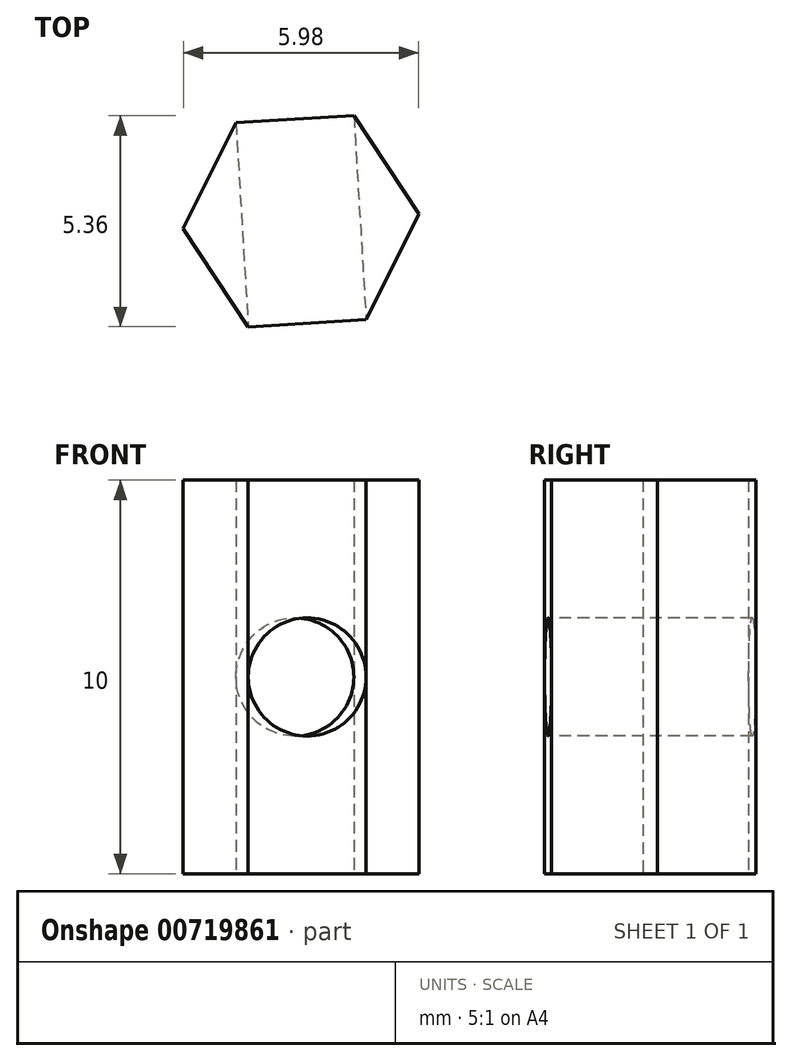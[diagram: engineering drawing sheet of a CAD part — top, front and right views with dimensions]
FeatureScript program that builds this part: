
annotation { "Feature Type Name" : "Feature", "Feature Type Description" : "" }
export const myFeature = defineFeature(function(context is Context, id is Id, definition is map)
    precondition{}
    {
        {
            var Q0;
            Q0=qCreatedBy(makeId("Top.planeOp"),FACE);
            var sketch = newSketch(context, id + "F0", { "sketchPlane" : qUnion([Q0])});
            skCircle(sketch, "E0.cCircle", {"center": v(0, 0) * mm, "radius": 3 * mm, "construction": true});
            skLineSegment(sketch, "E0.0", {"start": v(1.65, -2.5) * mm, "end": v(-1.34, -2.68) * mm});
            skLineSegment(sketch, "E0.1", {"start": v(-1.34, -2.68) * mm, "end": v(-3, -0.18) * mm});
            skLineSegment(sketch, "E0.2", {"start": v(-3, -0.18) * mm, "end": v(-1.65, 2.5) * mm});
            skLineSegment(sketch, "E0.3", {"start": v(-1.65, 2.5) * mm, "end": v(1.34, 2.68) * mm});
            skLineSegment(sketch, "E0.4", {"start": v(1.34, 2.68) * mm, "end": v(3, 0.18) * mm});
            skLineSegment(sketch, "E0.5", {"start": v(3, 0.18) * mm, "end": v(1.65, -2.5) * mm});
            skSolve(sketch);
        }
        {
            var Q0;
            Q0=makeQuery(id+"F0.imprint","IMPRINT",FACE,{"disambiguationData":[TD([[makeQuery(id+"F0.imprint","IMPRINT",EDGE,{"derivedFrom":sQuery(id+"F0.wireOp",EDGE,"E0.0")}),-1.0]])]});
            extrude(context, id + "F1", {"entities" : qUnion([Q0]), "depth" : 10 * mm, "offsetDistance" : 25.4 * mm});
        }
        {
            var Q0;
            Q0=makeQuery(id+"F1.opExtrude","SWEPT_FACE",FACE,{"disambiguationData":[OSD([sQuery(id+"F0.wireOp",EDGE,"E0.0")])]});
            var sketch = newSketch(context, id + "F2", { "sketchPlane" : qUnion([Q0])});
            skLineSegment(sketch, "E1", {"start": v(1.5, 10) * mm, "end": v(1.5, 0) * mm, "construction": true});
            skLineSegment(sketch, "E2", {"start": v(1.5, 5) * mm, "end": v(-1.5, 5) * mm, "construction": true});
            skCircle(sketch, "E3", {"center": v(0, 5) * mm, "radius": 1.5 * mm});
            skSolve(sketch);
        }
        {
            var Q0;
            {var subQ0=sQuery(id+"F2.wireOp",EDGE,"E3");var subQ1=sQuery(id+"F0.wireOp",EDGE,"E0.0");var subQ2=makeQuery(id+"F2.imprint","INTERSECT",VERTEX,{"derivedFrom":[makeQuery(id+"F1.opExtrude","SWEPT_EDGE",EDGE,{"disambiguationData":[OSD([subQ1,sQuery(id+"F0.wireOp",EDGE,"E0.5")])]}),subQ0]});Q0=makeQuery(id+"F2.imprint","IMPRINT",FACE,{"disambiguationData":[TD([[makeQuery(id+"F2.imprint","IMPRINT",EDGE,{"disambiguationData":[TD([[subQ2,-1.0]])],"derivedFrom":subQ0}),1.0]])]});}
            extrude(context, id + "F3", {"entities" : qUnion([Q0]), "operationType" : NewBodyOperationType.REMOVE, "endBound" : BoundingType.UP_TO_NEXT, "oppositeDirection" : true, "depth" : 25.4 * mm, "offsetDistance" : 25.4 * mm});
        }
    });
